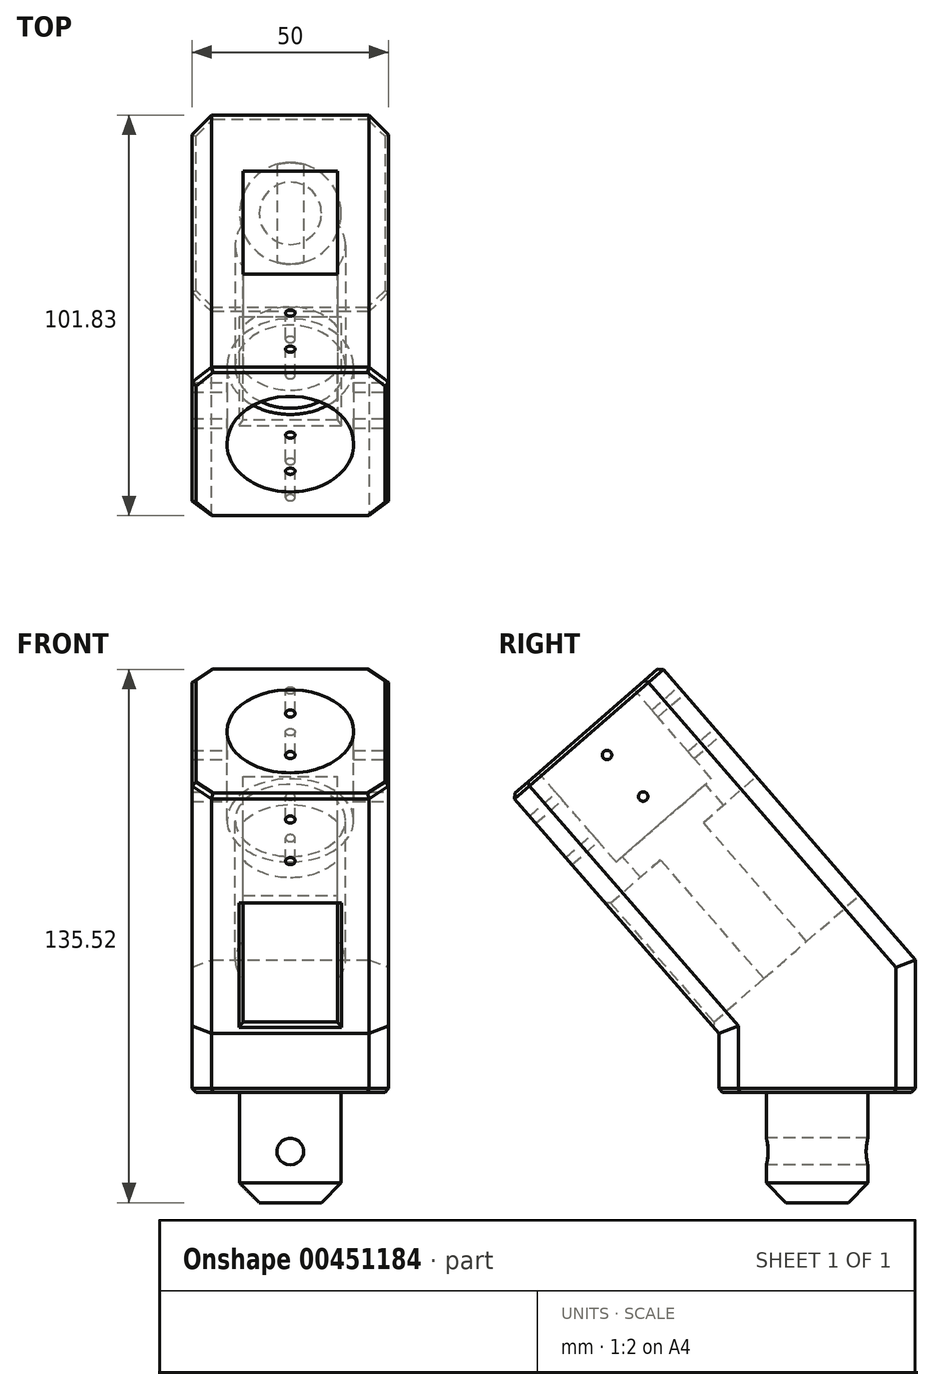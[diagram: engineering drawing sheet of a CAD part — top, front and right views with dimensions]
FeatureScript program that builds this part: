
annotation { "Feature Type Name" : "Feature", "Feature Type Description" : "" }
export const myFeature = defineFeature(function(context is Context, id is Id, definition is map)
    precondition{}
    {
        {
            var Q0;
            Q0=qCreatedBy(makeId("Top.planeOp"),FACE);
            var sketch = newSketch(context, id + "F0", { "sketchPlane" : qUnion([Q0])});
            skLineSegment(sketch, "E0.bottom", {"start": v(25, 25) * mm, "end": v(-25, 25) * mm});
            skLineSegment(sketch, "E0.top", {"start": v(25, -25) * mm, "end": v(-25, -25) * mm});
            skLineSegment(sketch, "E0.left", {"start": v(25, 25) * mm, "end": v(25, -25) * mm});
            skLineSegment(sketch, "E0.right", {"start": v(-25, 25) * mm, "end": v(-25, -25) * mm});
            skPoint(sketch, "E0.middle", {"position": v(0, 0) * mm});
            skSolve(sketch);
        }
        {
            var Q0;
            Q0 = qSketchRegion(id + "F0", true);
            extrude(context, id + "F1", {"entities" : qUnion([Q0]), "depth" : 15 * mm, "offsetDistance" : 25 * mm});
        }
        {
            var Q0;
            Q0=makeQuery(id+"F1.opExtrude","CAP_FACE",FACE,{"disambiguationData":[OSD([sQuery(id+"F0.wireOp",EDGE,"E0.bottom"),sQuery(id+"F0.wireOp",EDGE,"E0.top"),sQuery(id+"F0.wireOp",EDGE,"E0.left"),sQuery(id+"F0.wireOp",EDGE,"E0.right")])],"isStart":true});
            var sketch = newSketch(context, id + "F2", { "sketchPlane" : qUnion([Q0])});
            skCircle(sketch, "E1", {"center": v(0, 0) * mm, "radius": 12.9 * mm});
            skSolve(sketch);
        }
        {
            var Q0;
            Q0 = qSketchRegion(id + "F2", true);
            extrude(context, id + "F3", {"entities" : qUnion([Q0]), "operationType" : NewBodyOperationType.ADD, "depth" : 28 * mm, "offsetDistance" : 25 * mm});
        }
        {
            var Q0;
            Q0=qCreatedBy(makeId("Front.planeOp"),FACE);
            var sketch = newSketch(context, id + "F4", { "sketchPlane" : qUnion([Q0])});
            skCircle(sketch, "E2", {"center": v(0, -15) * mm, "radius": 3.4 * mm});
            skSolve(sketch);
        }
        {
            var Q0;
            Q0 = qSketchRegion(id + "F4", true);
            extrude(context, id + "F5", {"entities" : qUnion([Q0]), "operationType" : NewBodyOperationType.REMOVE, "oppositeDirection" : true, "depth" : 42 * mm, "offsetDistance" : 25 * mm, "symmetric" : true});
        }
        {
            var Q0;
            Q0=makeQuery(id+"F1.opExtrude","SWEPT_FACE",FACE,{"disambiguationData":[OSD([sQuery(id+"F0.wireOp",EDGE,"E0.left")])]});
            var sketch = newSketch(context, id + "F6", { "sketchPlane" : qUnion([Q0])});
            skLineSegment(sketch, "E3", {"start": v(-25, 15) * mm, "end": v(-77.48, 75.38) * mm});
            skLineSegment(sketch, "E4", {"start": v(-77.48, 75.38) * mm, "end": v(-39.75, 108.18) * mm});
            skLineSegment(sketch, "E5", {"start": v(25, 15) * mm, "end": v(-25, 15) * mm});
            skLineSegment(sketch, "E6", {"start": v(-39.75, 108.18) * mm, "end": v(25, 33.7) * mm});
            skLineSegment(sketch, "E7", {"start": v(25, 33.7) * mm, "end": v(25, 15) * mm});
            skLineSegment(sketch, "E8", {"start": v(-25, 15) * mm, "end": v(12.74, 47.8) * mm, "construction": true});
            skSolve(sketch);
        }
        {
            var Q0;
            Q0 = qSketchRegion(id + "F6", true);
            extrude(context, id + "F7", {"entities" : qUnion([Q0]), "operationType" : NewBodyOperationType.ADD, "oppositeDirection" : true, "depth" : 50 * mm, "offsetDistance" : 25 * mm});
        }
        {
            var Q0;
            Q0=makeQuery(id+"F7.opExtrude","SWEPT_FACE",FACE,{"disambiguationData":[OSD([sQuery(id+"F6.wireOp",EDGE,"E4")])]});
            var sketch = newSketch(context, id + "F8", { "sketchPlane" : qUnion([Q0])});
            skCircle(sketch, "E9", {"center": v(0, 15.97) * mm, "radius": 14 * mm});
            skSolve(sketch);
        }
        {
            var Q0;
            Q0 = qSketchRegion(id + "F8", true);
            extrude(context, id + "F9", {"entities" : qUnion([Q0]), "operationType" : NewBodyOperationType.REMOVE, "oppositeDirection" : true, "depth" : 77 * mm, "offsetDistance" : 25 * mm});
        }
        {
            var Q0;
            Q0=makeQuery(id+"F7.opExtrude","SWEPT_FACE",FACE,{"disambiguationData":[OSD([sQuery(id+"F6.wireOp",EDGE,"E4")])]});
            var sketch = newSketch(context, id + "F10", { "sketchPlane" : qUnion([Q0])});
            skCircle(sketch, "E10", {"center": v(0, 15.97) * mm, "radius": 16.1 * mm});
            skSolve(sketch);
        }
        {
            var Q0;
            Q0 = qSketchRegion(id + "F10", true);
            extrude(context, id + "F11", {"entities" : qUnion([Q0]), "operationType" : NewBodyOperationType.REMOVE, "oppositeDirection" : true, "depth" : 30 * mm, "offsetDistance" : 25 * mm});
        }
        {
            var Q0;
            Q0=makeQuery(id+"F7.opExtrude","SWEPT_FACE",FACE,{"disambiguationData":[OSD([sQuery(id+"F6.wireOp",EDGE,"E6")])]});
            var sketch = newSketch(context, id + "F12", { "sketchPlane" : qUnion([Q0])});
            skLineSegment(sketch, "E11.bottom", {"start": v(12, 30.72) * mm, "end": v(-12, 30.72) * mm});
            skLineSegment(sketch, "E11.top", {"start": v(12, 70.72) * mm, "end": v(-12, 70.72) * mm});
            skLineSegment(sketch, "E11.left", {"start": v(12, 30.72) * mm, "end": v(12, 70.72) * mm});
            skLineSegment(sketch, "E11.right", {"start": v(-12, 30.72) * mm, "end": v(-12, 70.72) * mm});
            skPoint(sketch, "E11.middle", {"position": v(0, 50.72) * mm});
            skSolve(sketch);
        }
        {
            var Q0;
            Q0 = qSketchRegion(id + "F12", true);
            extrude(context, id + "F13", {"entities" : qUnion([Q0]), "operationType" : NewBodyOperationType.REMOVE, "endBound" : BoundingType.THROUGH_ALL, "oppositeDirection" : true, "depth" : 25 * mm, "offsetDistance" : 25 * mm});
        }
        {
            var Q0;
            Q0=makeQuery(id+"F7.opExtrude","SWEPT_FACE",FACE,{"disambiguationData":[OSD([sQuery(id+"F6.wireOp",EDGE,"E6")])]});
            var sketch = newSketch(context, id + "F14", { "sketchPlane" : qUnion([Q0])});
            skCircle(sketch, "E12", {"center": v(0, 99.72) * mm, "radius": 1.2 * mm});
            skCircle(sketch, "E13", {"center": v(0, 85.72) * mm, "radius": 1.2 * mm});
            skSolve(sketch);
        }
        {
            var Q0;
            Q0 = qSketchRegion(id + "F14", true);
            extrude(context, id + "F15", {"entities" : qUnion([Q0]), "operationType" : NewBodyOperationType.REMOVE, "endBound" : BoundingType.THROUGH_ALL, "oppositeDirection" : true, "depth" : 25 * mm, "offsetDistance" : 25 * mm});
        }
        {
            var Q0;
            Q0=makeQuery(id+"F7.boolean.opBoolean","MERGE",FACE,{"derivedFrom":[makeQuery(id+"F1.opExtrude","SWEPT_FACE",FACE,{"disambiguationData":[OSD([sQuery(id+"F0.wireOp",EDGE,"E0.left")])]}),makeQuery(id+"F7.opExtrude","CAP_FACE",FACE,{"disambiguationData":[OSD([sQuery(id+"F6.wireOp",EDGE,"E3"),sQuery(id+"F6.wireOp",EDGE,"E4"),sQuery(id+"F6.wireOp",EDGE,"E5"),sQuery(id+"F6.wireOp",EDGE,"E6"),sQuery(id+"F6.wireOp",EDGE,"E7")])],"isStart":true})]});
            var sketch = newSketch(context, id + "F16", { "sketchPlane" : qUnion([Q0])});
            skCircle(sketch, "E14", {"center": v(-53.37, 85.74) * mm, "radius": 1.2 * mm});
            skCircle(sketch, "E15", {"center": v(-44.18, 75.17) * mm, "radius": 1.2 * mm});
            skLineSegment(sketch, "E16", {"start": v(-58.62, 91.78) * mm, "end": v(-35.28, 64.94) * mm, "construction": true});
            skSolve(sketch);
        }
        {
            var Q0;
            Q0 = qSketchRegion(id + "F16", true);
            extrude(context, id + "F17", {"entities" : qUnion([Q0]), "operationType" : NewBodyOperationType.REMOVE, "endBound" : BoundingType.THROUGH_ALL, "oppositeDirection" : true, "depth" : 25 * mm, "offsetDistance" : 25 * mm});
        }
        {
            var Q0;
            Q0=makeQuery(id+"F3.opExtrude","CAP_EDGE",EDGE,{"disambiguationData":[OSD([sQuery(id+"F2.wireOp",EDGE,"E1")])],"isStart":false});
            var Q1;
            Q1=makeQuery(id+"F7.opExtrude","CAP_EDGE",EDGE,{"disambiguationData":[OSD([sQuery(id+"F6.wireOp",EDGE,"E3")])],"isStart":true});
            var Q2;
            Q2=makeQuery(id+"F1.opExtrude","SWEPT_EDGE",EDGE,{"disambiguationData":[OSD([sQuery(id+"F0.wireOp",EDGE,"E0.top"),sQuery(id+"F0.wireOp",EDGE,"E0.left")])]});
            var Q3;
            Q3=makeQuery(id+"F7.boolean.opBoolean","MERGE",EDGE,{"derivedFrom":[makeQuery(id+"F1.opExtrude","SWEPT_EDGE",EDGE,{"disambiguationData":[OSD([sQuery(id+"F0.wireOp",EDGE,"E0.bottom"),sQuery(id+"F0.wireOp",EDGE,"E0.left")])]}),makeQuery(id+"F7.opExtrude","CAP_EDGE",EDGE,{"disambiguationData":[OSD([sQuery(id+"F6.wireOp",EDGE,"E7")])],"isStart":true})]});
            var Q4;
            Q4=makeQuery(id+"F7.opExtrude","CAP_EDGE",EDGE,{"disambiguationData":[OSD([sQuery(id+"F6.wireOp",EDGE,"E6")])],"isStart":true});
            var Q5;
            Q5=makeQuery(id+"F7.boolean.opBoolean","MERGE",EDGE,{"derivedFrom":[makeQuery(id+"F1.opExtrude","SWEPT_EDGE",EDGE,{"disambiguationData":[OSD([sQuery(id+"F0.wireOp",EDGE,"E0.bottom"),sQuery(id+"F0.wireOp",EDGE,"E0.right")])]}),makeQuery(id+"F7.opExtrude","CAP_EDGE",EDGE,{"disambiguationData":[OSD([sQuery(id+"F6.wireOp",EDGE,"E7")])],"isStart":false})]});
            var Q6;
            Q6=makeQuery(id+"F7.opExtrude","CAP_EDGE",EDGE,{"disambiguationData":[OSD([sQuery(id+"F6.wireOp",EDGE,"E6")])],"isStart":false});
            var Q7;
            Q7=makeQuery(id+"F1.opExtrude","SWEPT_EDGE",EDGE,{"disambiguationData":[OSD([sQuery(id+"F0.wireOp",EDGE,"E0.top"),sQuery(id+"F0.wireOp",EDGE,"E0.right")])]});
            var Q8;
            Q8=makeQuery(id+"F7.opExtrude","CAP_EDGE",EDGE,{"disambiguationData":[OSD([sQuery(id+"F6.wireOp",EDGE,"E3")])],"isStart":false});
            chamfer(context, id + "F18", {"entities" : qUnion([Q0, Q1, Q2, Q3, Q4, Q5, Q6, Q7, Q8]), "width" : 5 * mm, "tangentPropagation" : true});
        }
        {
            var Q0;
            Q0=makeQuery(id+"F11.boolean.opBoolean","COPY",EDGE,{"derivedFrom":makeQuery(id+"F11.opExtrude","CAP_EDGE",EDGE,{"disambiguationData":[OSD([sQuery(id+"F10.wireOp",EDGE,"E10")])],"isStart":true})});
            var Q1;
            Q1=makeQuery(id+"F13.boolean.opBoolean","INTERSECT",EDGE,{"derivedFrom":[makeQuery(id+"F7.opExtrude","SWEPT_FACE",FACE,{"disambiguationData":[OSD([sQuery(id+"F6.wireOp",EDGE,"E3")])]}),makeQuery(id+"F13.opExtrude","SWEPT_FACE",FACE,{"disambiguationData":[OSD([sQuery(id+"F12.wireOp",EDGE,"E11.right")])]})]});
            var Q2;
            Q2=makeQuery(id+"F13.boolean.opBoolean","INTERSECT",EDGE,{"derivedFrom":[makeQuery(id+"F7.opExtrude","SWEPT_FACE",FACE,{"disambiguationData":[OSD([sQuery(id+"F6.wireOp",EDGE,"E3")])]}),makeQuery(id+"F13.opExtrude","SWEPT_FACE",FACE,{"disambiguationData":[OSD([sQuery(id+"F12.wireOp",EDGE,"E11.top")])]})]});
            var Q3;
            Q3=makeQuery(id+"F13.boolean.opBoolean","INTERSECT",EDGE,{"derivedFrom":[makeQuery(id+"F7.opExtrude","SWEPT_FACE",FACE,{"disambiguationData":[OSD([sQuery(id+"F6.wireOp",EDGE,"E3")])]}),makeQuery(id+"F13.opExtrude","SWEPT_FACE",FACE,{"disambiguationData":[OSD([sQuery(id+"F12.wireOp",EDGE,"E11.left")])]})]});
            var Q4;
            Q4=makeQuery(id+"F13.boolean.opBoolean","INTERSECT",EDGE,{"derivedFrom":[makeQuery(id+"F7.opExtrude","SWEPT_FACE",FACE,{"disambiguationData":[OSD([sQuery(id+"F6.wireOp",EDGE,"E3")])]}),makeQuery(id+"F13.opExtrude","SWEPT_FACE",FACE,{"disambiguationData":[OSD([sQuery(id+"F12.wireOp",EDGE,"E11.bottom")])]})]});
            var Q5;
            Q5=makeQuery(id+"F13.boolean.opBoolean","COPY",EDGE,{"derivedFrom":makeQuery(id+"F13.opExtrude","CAP_EDGE",EDGE,{"disambiguationData":[OSD([sQuery(id+"F12.wireOp",EDGE,"E11.bottom")])],"isStart":true})});
            var Q6;
            Q6=makeQuery(id+"F13.boolean.opBoolean","COPY",EDGE,{"derivedFrom":makeQuery(id+"F13.opExtrude","CAP_EDGE",EDGE,{"disambiguationData":[OSD([sQuery(id+"F12.wireOp",EDGE,"E11.left")])],"isStart":true})});
            var Q7;
            Q7=makeQuery(id+"F13.boolean.opBoolean","COPY",EDGE,{"derivedFrom":makeQuery(id+"F13.opExtrude","CAP_EDGE",EDGE,{"disambiguationData":[OSD([sQuery(id+"F12.wireOp",EDGE,"E11.right")])],"isStart":true})});
            var Q8;
            Q8=makeQuery(id+"F13.boolean.opBoolean","COPY",EDGE,{"derivedFrom":makeQuery(id+"F13.opExtrude","CAP_EDGE",EDGE,{"disambiguationData":[OSD([sQuery(id+"F12.wireOp",EDGE,"E11.top")])],"isStart":true})});
            var Q9;
            Q9=makeQuery(id+"F1.opExtrude","CAP_EDGE",EDGE,{"disambiguationData":[OSD([sQuery(id+"F0.wireOp",EDGE,"E0.right")])],"isStart":true});
            var Q10;
            {var subQ0=sQuery(id+"F0.wireOp",EDGE,"E0.right");var subQ1=sQuery(id+"F0.wireOp",EDGE,"E0.top");Q10=makeQuery(id+"F18.opChamfer","BLEND_EDGE",EDGE,{"blendedFrom":[makeQuery(id+"F1.opExtrude","SWEPT_EDGE",EDGE,{"disambiguationData":[OSD([subQ1,subQ0])]}),makeQuery(id+"F1.opExtrude","CAP_FACE",FACE,{"disambiguationData":[OSD([sQuery(id+"F0.wireOp",EDGE,"E0.bottom"),subQ1,sQuery(id+"F0.wireOp",EDGE,"E0.left"),subQ0])],"isStart":true})],"blendedInto":[makeQuery(id+"F1.opExtrude","CAP_FACE",FACE,{"disambiguationData":[OSD([sQuery(id+"F0.wireOp",EDGE,"E0.bottom"),subQ1,sQuery(id+"F0.wireOp",EDGE,"E0.left"),subQ0])],"isStart":true})]});}
            var Q11;
            Q11=makeQuery(id+"F1.opExtrude","CAP_EDGE",EDGE,{"disambiguationData":[OSD([sQuery(id+"F0.wireOp",EDGE,"E0.top")])],"isStart":true});
            var Q12;
            {var subQ0=sQuery(id+"F0.wireOp",EDGE,"E0.left");var subQ1=sQuery(id+"F0.wireOp",EDGE,"E0.top");Q12=makeQuery(id+"F18.opChamfer","BLEND_EDGE",EDGE,{"blendedFrom":[makeQuery(id+"F1.opExtrude","SWEPT_EDGE",EDGE,{"disambiguationData":[OSD([subQ1,subQ0])]}),makeQuery(id+"F1.opExtrude","CAP_FACE",FACE,{"disambiguationData":[OSD([sQuery(id+"F0.wireOp",EDGE,"E0.bottom"),subQ1,subQ0,sQuery(id+"F0.wireOp",EDGE,"E0.right")])],"isStart":true})],"blendedInto":[makeQuery(id+"F1.opExtrude","CAP_FACE",FACE,{"disambiguationData":[OSD([sQuery(id+"F0.wireOp",EDGE,"E0.bottom"),subQ1,subQ0,sQuery(id+"F0.wireOp",EDGE,"E0.right")])],"isStart":true})]});}
            var Q13;
            Q13=makeQuery(id+"F1.opExtrude","CAP_EDGE",EDGE,{"disambiguationData":[OSD([sQuery(id+"F0.wireOp",EDGE,"E0.left")])],"isStart":true});
            var Q14;
            {var subQ0=sQuery(id+"F0.wireOp",EDGE,"E0.left");var subQ1=sQuery(id+"F0.wireOp",EDGE,"E0.bottom");Q14=makeQuery(id+"F18.opChamfer","BLEND_EDGE",EDGE,{"blendedFrom":[makeQuery(id+"F7.boolean.opBoolean","MERGE",EDGE,{"derivedFrom":[makeQuery(id+"F1.opExtrude","SWEPT_EDGE",EDGE,{"disambiguationData":[OSD([subQ1,subQ0])]}),makeQuery(id+"F7.opExtrude","CAP_EDGE",EDGE,{"disambiguationData":[OSD([sQuery(id+"F6.wireOp",EDGE,"E7")])],"isStart":true})]}),makeQuery(id+"F1.opExtrude","CAP_FACE",FACE,{"disambiguationData":[OSD([subQ1,sQuery(id+"F0.wireOp",EDGE,"E0.top"),subQ0,sQuery(id+"F0.wireOp",EDGE,"E0.right")])],"isStart":true})],"blendedInto":[makeQuery(id+"F1.opExtrude","CAP_FACE",FACE,{"disambiguationData":[OSD([subQ1,sQuery(id+"F0.wireOp",EDGE,"E0.top"),subQ0,sQuery(id+"F0.wireOp",EDGE,"E0.right")])],"isStart":true})]});}
            var Q15;
            Q15=makeQuery(id+"F1.opExtrude","CAP_EDGE",EDGE,{"disambiguationData":[OSD([sQuery(id+"F0.wireOp",EDGE,"E0.bottom")])],"isStart":true});
            var Q16;
            {var subQ0=sQuery(id+"F0.wireOp",EDGE,"E0.right");var subQ1=sQuery(id+"F0.wireOp",EDGE,"E0.bottom");Q16=makeQuery(id+"F18.opChamfer","BLEND_EDGE",EDGE,{"blendedFrom":[makeQuery(id+"F7.boolean.opBoolean","MERGE",EDGE,{"derivedFrom":[makeQuery(id+"F1.opExtrude","SWEPT_EDGE",EDGE,{"disambiguationData":[OSD([subQ1,subQ0])]}),makeQuery(id+"F7.opExtrude","CAP_EDGE",EDGE,{"disambiguationData":[OSD([sQuery(id+"F6.wireOp",EDGE,"E7")])],"isStart":false})]}),makeQuery(id+"F1.opExtrude","CAP_FACE",FACE,{"disambiguationData":[OSD([subQ1,sQuery(id+"F0.wireOp",EDGE,"E0.top"),sQuery(id+"F0.wireOp",EDGE,"E0.left"),subQ0])],"isStart":true})],"blendedInto":[makeQuery(id+"F1.opExtrude","CAP_FACE",FACE,{"disambiguationData":[OSD([subQ1,sQuery(id+"F0.wireOp",EDGE,"E0.top"),sQuery(id+"F0.wireOp",EDGE,"E0.left"),subQ0])],"isStart":true})]});}
            var Q17;
            Q17=makeQuery(id+"F7.opExtrude","SWEPT_EDGE",EDGE,{"disambiguationData":[OSD([sQuery(id+"F6.wireOp",EDGE,"E3"),sQuery(id+"F6.wireOp",EDGE,"E4")])]});
            var Q18;
            Q18=makeQuery(id+"F18.opChamfer","BLEND_EDGE",EDGE,{"blendedFrom":[makeQuery(id+"F7.opExtrude","CAP_EDGE",EDGE,{"disambiguationData":[OSD([sQuery(id+"F6.wireOp",EDGE,"E3")])],"isStart":false}),makeQuery(id+"F7.opExtrude","SWEPT_FACE",FACE,{"disambiguationData":[OSD([sQuery(id+"F6.wireOp",EDGE,"E4")])]})],"blendedInto":[makeQuery(id+"F7.opExtrude","SWEPT_FACE",FACE,{"disambiguationData":[OSD([sQuery(id+"F6.wireOp",EDGE,"E4")])]})]});
            var Q19;
            Q19=makeQuery(id+"F7.opExtrude","CAP_EDGE",EDGE,{"disambiguationData":[OSD([sQuery(id+"F6.wireOp",EDGE,"E4")])],"isStart":false});
            var Q20;
            Q20=makeQuery(id+"F7.opExtrude","CAP_EDGE",EDGE,{"disambiguationData":[OSD([sQuery(id+"F6.wireOp",EDGE,"E4")])],"isStart":true});
            var Q21;
            Q21=makeQuery(id+"F18.opChamfer","BLEND_EDGE",EDGE,{"blendedFrom":[makeQuery(id+"F7.opExtrude","CAP_EDGE",EDGE,{"disambiguationData":[OSD([sQuery(id+"F6.wireOp",EDGE,"E3")])],"isStart":true}),makeQuery(id+"F7.opExtrude","SWEPT_FACE",FACE,{"disambiguationData":[OSD([sQuery(id+"F6.wireOp",EDGE,"E4")])]})],"blendedInto":[makeQuery(id+"F7.opExtrude","SWEPT_FACE",FACE,{"disambiguationData":[OSD([sQuery(id+"F6.wireOp",EDGE,"E4")])]})]});
            var Q22;
            Q22=makeQuery(id+"F18.opChamfer","BLEND_EDGE",EDGE,{"blendedFrom":[makeQuery(id+"F7.opExtrude","CAP_EDGE",EDGE,{"disambiguationData":[OSD([sQuery(id+"F6.wireOp",EDGE,"E6")])],"isStart":true}),makeQuery(id+"F7.opExtrude","SWEPT_FACE",FACE,{"disambiguationData":[OSD([sQuery(id+"F6.wireOp",EDGE,"E4")])]})],"blendedInto":[makeQuery(id+"F7.opExtrude","SWEPT_FACE",FACE,{"disambiguationData":[OSD([sQuery(id+"F6.wireOp",EDGE,"E4")])]})]});
            var Q23;
            Q23=makeQuery(id+"F7.opExtrude","SWEPT_EDGE",EDGE,{"disambiguationData":[OSD([sQuery(id+"F6.wireOp",EDGE,"E4"),sQuery(id+"F6.wireOp",EDGE,"E6")])]});
            var Q24;
            Q24=makeQuery(id+"F18.opChamfer","BLEND_EDGE",EDGE,{"blendedFrom":[makeQuery(id+"F7.opExtrude","CAP_EDGE",EDGE,{"disambiguationData":[OSD([sQuery(id+"F6.wireOp",EDGE,"E6")])],"isStart":false}),makeQuery(id+"F7.opExtrude","SWEPT_FACE",FACE,{"disambiguationData":[OSD([sQuery(id+"F6.wireOp",EDGE,"E4")])]})],"blendedInto":[makeQuery(id+"F7.opExtrude","SWEPT_FACE",FACE,{"disambiguationData":[OSD([sQuery(id+"F6.wireOp",EDGE,"E4")])]})]});
            chamfer(context, id + "F19", {"entities" : qUnion([Q0, Q1, Q2, Q3, Q4, Q5, Q6, Q7, Q8, Q9, Q10, Q11, Q12, Q13, Q14, Q15, Q16, Q17, Q18, Q19, Q20, Q21, Q22, Q23, Q24]), "width" : 1 * mm, "tangentPropagation" : true});
        }
    });
